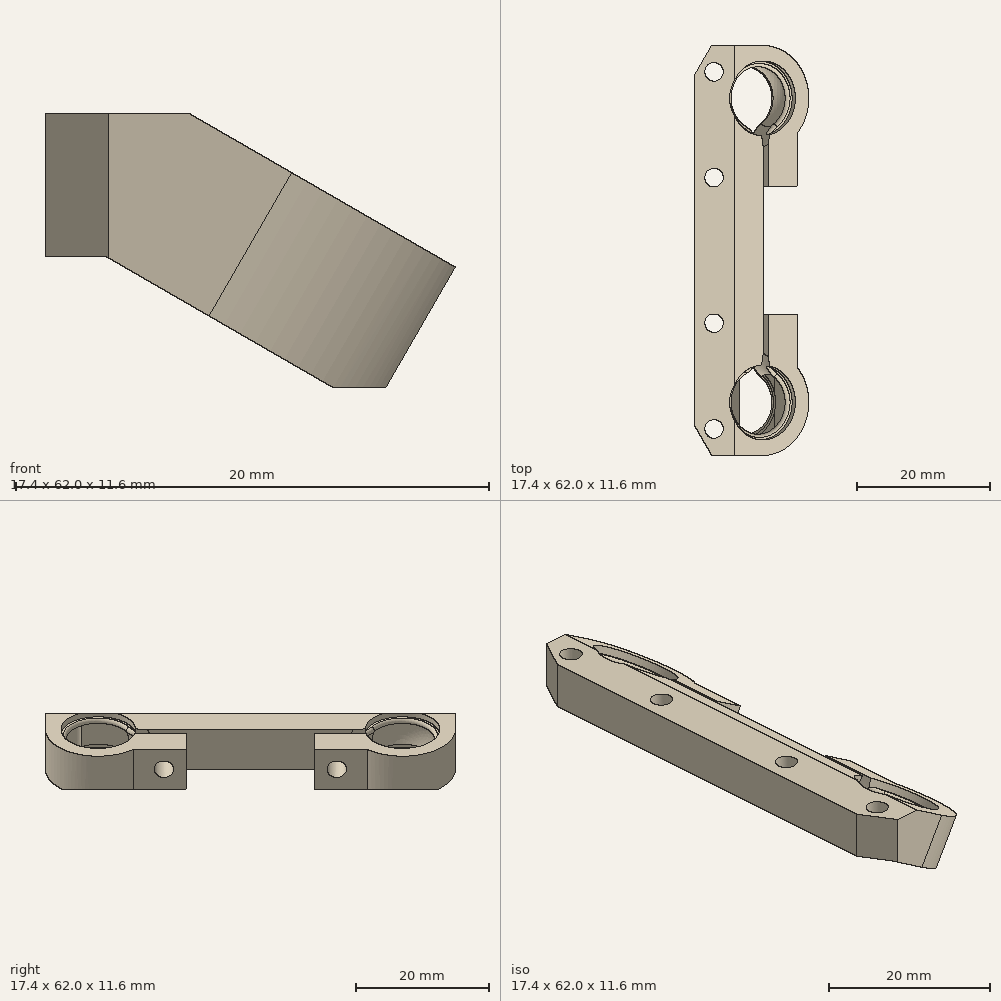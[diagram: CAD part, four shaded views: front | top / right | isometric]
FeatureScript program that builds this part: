
annotation { "Feature Type Name" : "Feature", "Feature Type Description" : "" }
export const myFeature = defineFeature(function(context is Context, id is Id, definition is map)
    precondition{}
    {
        {
            assignVariable(context, id + "F0", {"name" : "balld", "anyValue" : 10});
        }
        {
            assignVariable(context, id + "F1", {"name" : "bushd", "anyValue" : 8});
        }
        {
            var Q0;
            Q0=qCreatedBy(makeId("Top.planeOp"),FACE);
            var sketch = newSketch(context, id + "F2", { "sketchPlane" : qUnion([Q0])});
            skLineSegment(sketch, "E0", {"start": v(0, -23) * mm, "end": v(0, 23) * mm});
            skCircle(sketch, "E1", {"center": v(0, -23) * mm, "radius": 5.15 * mm});
            skArc(sketch, "E2", {"start": v(0, -31) * mm, "mid": v(7.31, -26.24) * mm, "end": v(5.92, -17.62) * mm});
            skLineSegment(sketch, "E3", {"start": v(-5.15, -23) * mm, "end": v(5.15, -23) * mm});
            skLineSegment(sketch, "E4", {"start": v(-8, -23) * mm, "end": v(-8, 0) * mm});
            skLineSegment(sketch, "E5", {"start": v(-8, 0) * mm, "end": v(0, 0) * mm});
            skLineSegment(sketch, "E6", {"start": v(0, -9.62) * mm, "end": v(5.92, -9.62) * mm});
            skLineSegment(sketch, "E7", {"start": v(5.92, -9.62) * mm, "end": v(5.92, -17.62) * mm});
            skLineSegment(sketch, "E8", {"start": v(1, -23) * mm, "end": v(1, -9.62) * mm});
            skCircle(sketch, "E9.0", {"center": v(0, -23) * mm, "radius": 5.65 * mm});
            skLineSegment(sketch, "E10", {"start": v(-8, -23) * mm, "end": v(-8, -31) * mm});
            skLineSegment(sketch, "E11", {"start": v(-8, -31) * mm, "end": v(2.55, -31) * mm});
            skSolve(sketch);
        }
        {
            var Q0;
            Q0=makeQuery(id+"F2.imprint","IMPRINT",FACE,{"disambiguationData":[TD([[makeQuery(id+"F2.imprint","IMPRINT",EDGE,{"derivedFrom":sQuery(id+"F2.wireOp",EDGE,"E2")}),1.0]])]});
            var Q1;
            {var subQ0=sQuery(id+"F2.wireOp",EDGE,"E3");Q1=makeQuery(id+"F2.imprint","IMPRINT",FACE,{"disambiguationData":[TD([[makeQuery(id+"F2.imprint","IMPRINT",EDGE,{"derivedFrom":subQ0}),1.0]])]});}
            var Q2;
            {var subQ0=sQuery(id+"F2.wireOp",EDGE,"E3");Q2=makeQuery(id+"F2.imprint","IMPRINT",FACE,{"disambiguationData":[TD([[makeQuery(id+"F2.imprint","IMPRINT",EDGE,{"derivedFrom":subQ0}),-1.0]])]});}
            var Q3;
            {var subQ0=sQuery(id+"F2.wireOp",EDGE,"0A8tKCgS-ejaw-YyMs-Dn46-rruMUtFQQFLV");Q3=makeQuery(id+"F2.imprint","IMPRINT",FACE,{"disambiguationData":[TD([[makeQuery(id+"F2.imprint","IMPRINT",EDGE,{"derivedFrom":subQ0}),1.0]])]});}
            var Q4;
            {var subQ1=sQuery(id+"F2.wireOp",EDGE,"E1");var subQ8=sQuery(id+"F2.wireOp",EDGE,"E0");var subQ9=makeQuery(id+"F2.imprint","INTERSECT",VERTEX,{"derivedFrom":[subQ8,subQ1]});Q4=makeQuery(id+"F2.imprint","IMPRINT",FACE,{"disambiguationData":[TD([[makeQuery(id+"F2.imprint","IMPRINT",EDGE,{"disambiguationData":[TD([[subQ9,-1.0]])],"derivedFrom":subQ8}),1.0]])]});}
            extrude(context, id + "F3", {"entities" : qUnion([Q0, Q1, Q2, Q3, Q4]), "endBound" : BoundingType.SYMMETRIC, "depth" : (getVariable(context, 'balld') / 2) * mm});
        }
        {
            var Q0;
            Q0=makeQuery(id+"F2.imprint","IMPRINT",FACE,{"disambiguationData":[TD([[makeQuery(id+"F2.imprint","IMPRINT",EDGE,{"derivedFrom":sQuery(id+"F2.wireOp",EDGE,"E2")}),1.0]])]});
            extrude(context, id + "F4", {"entities" : qUnion([Q0]), "operationType" : NewBodyOperationType.ADD, "endBound" : BoundingType.SYMMETRIC, "depth" : 7 * mm});
        }
        {
            var Q0;
            {var subQ0=sQuery(id+"F2.wireOp",EDGE,"E7");Q0=makeQuery(id+"F4.boolean.opBoolean","MERGE",FACE,{"derivedFrom":[makeQuery(id+"F3.opExtrude","SWEPT_FACE",FACE,{"disambiguationData":[OSD([subQ0])]}),makeQuery(id+"F4.opExtrude","SWEPT_FACE",FACE,{"disambiguationData":[OSD([subQ0])]})]});}
            var sketch = newSketch(context, id + "F5", { "sketchPlane" : qUnion([Q0])});
            skCircle(sketch, "E12", {"center": v(-13.07, 0) * mm, "radius": 1.45 * mm});
            skPoint(sketch, "E12.centerSnap0", {"position": v(-9.62, 0) * mm});
            skSolve(sketch);
        }
        {
            var Q0;
            Q0=makeQuery(id+"F5.imprint","IMPRINT",FACE,{"disambiguationData":[TD([[makeQuery(id+"F5.imprint","IMPRINT",EDGE,{"derivedFrom":sQuery(id+"F5.wireOp",EDGE,"E12")}),1.0]])]});
            extrude(context, id + "F6", {"entities" : qUnion([Q0]), "operationType" : NewBodyOperationType.REMOVE, "oppositeDirection" : true, "depth" : 11 * mm});
        }
        {
            var Q0;
            {var subQ0=sQuery(id+"F2.wireOp",EDGE,"E5");Q0=makeQuery(id+"F4.boolean.opBoolean","MERGE",FACE,{"derivedFrom":[makeQuery(id+"F3.opExtrude","SWEPT_FACE",FACE,{"disambiguationData":[OSD([subQ0])]}),makeQuery(id+"F4.opExtrude","SWEPT_FACE",FACE,{"disambiguationData":[OSD([subQ0])]})]});}
            var sketch = newSketch(context, id + "F7", { "sketchPlane" : qUnion([Q0])});
            skCircle(sketch, "E13", {"center": v(0, 0) * mm, "radius": 16.02 * mm});
            skSolve(sketch);
        }
        {
            var Q0;
            Q0=makeQuery(id+"F3.opExtrude","SWEPT_BODY",BODY,{"disambiguationData":[OSD([sQuery(id+"F2.wireOp",EDGE,"E0"),sQuery(id+"F2.wireOp",EDGE,"E2"),sQuery(id+"F2.wireOp",EDGE,"E3"),sQuery(id+"F2.wireOp",EDGE,"E4"),sQuery(id+"F2.wireOp",EDGE,"E5"),sQuery(id+"F2.wireOp",EDGE,"E6"),sQuery(id+"F2.wireOp",EDGE,"E7"),sQuery(id+"F2.wireOp",EDGE,"E8"),sQuery(id+"F2.wireOp",EDGE,"E10"),sQuery(id+"F2.wireOp",EDGE,"E11")])]});
            var Q1;
            Q1=sQuery(id+"F7.wireOp",EDGE,"E13");
            transform(context, id + "F8", {"entities" : qUnion([Q0]), "transformType" : TransformType.ROTATION, "transformAxis" : qUnion([Q1]), "angle" : 30 * degree, "makeCopy" : false});
        }
        {
            var Q0;
            {var subQ0=sQuery(id+"F2.wireOp",EDGE,"E5");Q0=makeQuery(id+"F4.boolean.opBoolean","MERGE",FACE,{"derivedFrom":[makeQuery(id+"F3.opExtrude","SWEPT_FACE",FACE,{"disambiguationData":[OSD([subQ0])]}),makeQuery(id+"F4.opExtrude","SWEPT_FACE",FACE,{"disambiguationData":[OSD([subQ0])]})]});}
            var sketch = newSketch(context, id + "F9", { "sketchPlane" : qUnion([Q0])});
            skLineSegment(sketch, "E14", {"start": v(-6.5, -6.08) * mm, "end": v(8.68, -6.08) * mm});
            skLineSegment(sketch, "E15", {"start": v(8.68, -6.08) * mm, "end": v(8.68, 5.56) * mm});
            skLineSegment(sketch, "E16", {"start": v(8.68, 5.56) * mm, "end": v(2.63, 5.56) * mm});
            skLineSegment(sketch, "E17", {"start": v(1.75, -3.03) * mm, "end": v(1.75, -6.08) * mm});
            skLineSegment(sketch, "E18.0", {"start": v(-5.18, -7.03) * mm, "end": v(1.75, -3.03) * mm});
            skLineSegment(sketch, "E19", {"start": v(-5.18, -7.03) * mm, "end": v(-8.68, -0.97) * mm});
            skSolve(sketch);
        }
        {
            var Q0;
            {var subQ3=sQuery(id+"F9.wireOp",EDGE,"E17");Q0=makeQuery(id+"F9.imprint","IMPRINT",FACE,{"disambiguationData":[TD([[makeQuery(id+"F9.imprint","IMPRINT",EDGE,{"derivedFrom":subQ3}),1.0]])]});}
            var Q1;
            {var subQ0=sQuery(id+"F9.wireOp",EDGE,"E15");var subQ5=sQuery(id+"F9.wireOp",EDGE,"E16");var subQ6=makeQuery(id+"F9.imprint","INTERSECT",VERTEX,{"derivedFrom":[subQ0,subQ5]});Q1=makeQuery(id+"F9.imprint","IMPRINT",FACE,{"disambiguationData":[TD([[makeQuery(id+"F9.imprint","IMPRINT",EDGE,{"disambiguationData":[TD([[subQ6,-1.0]])],"derivedFrom":subQ5}),1.0]])]});}
            var Q2;
            {var subQ0=sQuery(id+"F2.wireOp",EDGE,"E11");Q2=makeQuery(id+"F4.boolean.opBoolean","MERGE",FACE,{"derivedFrom":[makeQuery(id+"F3.opExtrude","SWEPT_FACE",FACE,{"disambiguationData":[OSD([subQ0])]}),makeQuery(id+"F4.opExtrude","SWEPT_FACE",FACE,{"disambiguationData":[OSD([subQ0])]})]});}
            extrude(context, id + "F10", {"entities" : qUnion([Q0, Q1]), "operationType" : NewBodyOperationType.ADD, "endBound" : BoundingType.UP_TO_SURFACE, "oppositeDirection" : true, "endBoundEntityFace" : qUnion([Q2]), "depth" : (30 + getVariable(context, 'bushd')) * mm});
        }
        {
            var Q0;
            {var subQ0=sQuery(id+"F2.wireOp",EDGE,"E3");var subQ1=sQuery(id+"F2.wireOp",EDGE,"E1");var subQ2=makeQuery(id+"F2.imprint","INTERSECT",VERTEX,{"disambiguationData":[OD(0.0)],"derivedFrom":[subQ1,subQ0]});Q0=makeQuery(id+"F2.imprint","IMPRINT",FACE,{"disambiguationData":[TD([[makeQuery(id+"F2.imprint","IMPRINT",EDGE,{"disambiguationData":[TD([[subQ2,-1.0]])],"derivedFrom":subQ1}),1.0]])]});}
            var Q1;
            Q1=sQuery(id+"F2.wireOp",EDGE,"E3");
            revolve(context, id + "F11", {"operationType" : NewBodyOperationType.REMOVE, "entities" : qUnion([Q0]), "axis" : qUnion([Q1]), "revolveType" : RevolveType.FULL, "oppositeDirection" : true});
        }
        {
            var Q0;
            {var subQ0=sQuery(id+"F2.wireOp",EDGE,"E3");var subQ1=sQuery(id+"F2.wireOp",EDGE,"E1");var subQ2=makeQuery(id+"F2.imprint","INTERSECT",VERTEX,{"disambiguationData":[OD(0.0)],"derivedFrom":[subQ1,subQ0]});Q0=makeQuery(id+"F2.imprint","IMPRINT",FACE,{"disambiguationData":[TD([[makeQuery(id+"F2.imprint","IMPRINT",EDGE,{"disambiguationData":[TD([[subQ2,-1.0]])],"derivedFrom":subQ1}),1.0]])]});}
            var Q1;
            Q1=sQuery(id+"F2.wireOp",EDGE,"E3");
            revolve(context, id + "F12", {"entities" : qUnion([Q0]), "axis" : qUnion([Q1]), "revolveType" : RevolveType.FULL});
        }
        {
            var Q0;
            Q0=makeQuery(id+"F11.boolean.opBoolean","INTERSECT",EDGE,{"derivedFrom":[makeQuery(id+"F3.opExtrude","SWEPT_FACE",FACE,{"disambiguationData":[OSD([sQuery(id+"F2.wireOp",EDGE,"E0")])]}),makeQuery(id+"F11.opRevolve","SWEPT_FACE",FACE,{"disambiguationData":[OSD([sQuery(id+"F2.wireOp",EDGE,"E1")])]})]});
            var Q1;
            Q1=makeQuery(id+"F11.boolean.opBoolean","INTERSECT",EDGE,{"derivedFrom":[makeQuery(id+"F3.opExtrude","SWEPT_FACE",FACE,{"disambiguationData":[OSD([sQuery(id+"F2.wireOp",EDGE,"E8")])]}),makeQuery(id+"F11.opRevolve","SWEPT_FACE",FACE,{"disambiguationData":[OSD([sQuery(id+"F2.wireOp",EDGE,"E1")])]})]});
            fillet(context, id + "F13", {"entities" : qUnion([Q0, Q1]), "radius" : 4 * mm, "tangentPropagation" : true, "allowEdgeOverflow" : false});
        }
        {
            var Q0;
            {var subQ0=sQuery(id+"F9.wireOp",EDGE,"E16");var subQ1=sQuery(id+"F2.wireOp",EDGE,"E5");var subQ2=makeQuery(id+"F4.opExtrude","CAP_EDGE",EDGE,{"disambiguationData":[OSD([subQ1])],"isStart":false});var subQ3=makeQuery(id+"F9.imprint","INTERSECT",VERTEX,{"derivedFrom":[subQ2,subQ0]});Q0=makeQuery(id+"F9.imprint","IMPRINT",FACE,{"disambiguationData":[TD([[makeQuery(id+"F9.imprint","IMPRINT",EDGE,{"disambiguationData":[TD([[subQ3,1.0]])],"derivedFrom":subQ0}),-1.0]])]});}
            var Q1;
            {var subQ0=sQuery(id+"F9.wireOp",EDGE,"E19");var subQ1=sQuery(id+"F9.wireOp",EDGE,"E14");var subQ2=makeQuery(id+"F9.imprint","INTERSECT",VERTEX,{"derivedFrom":[subQ1,subQ0]});Q1=makeQuery(id+"F9.imprint","IMPRINT",FACE,{"disambiguationData":[TD([[makeQuery(id+"F9.imprint","IMPRINT",EDGE,{"disambiguationData":[TD([[subQ2,-1.0]])],"derivedFrom":subQ1}),-1.0]])]});}
            extrude(context, id + "F14", {"entities" : qUnion([Q0, Q1]), "operationType" : NewBodyOperationType.REMOVE, "oppositeDirection" : true, "depth" : 46.37 * mm});
        }
        {
            var Q0;
            Q0=makeQuery(id+"F11.boolean.opBoolean","INTERSECT",EDGE,{"derivedFrom":[makeQuery(id+"F3.opExtrude","CAP_FACE",FACE,{"disambiguationData":[OSD([sQuery(id+"F2.wireOp",EDGE,"E0"),sQuery(id+"F2.wireOp",EDGE,"E2"),sQuery(id+"F2.wireOp",EDGE,"E3"),sQuery(id+"F2.wireOp",EDGE,"E4"),sQuery(id+"F2.wireOp",EDGE,"E5"),sQuery(id+"F2.wireOp",EDGE,"E6"),sQuery(id+"F2.wireOp",EDGE,"E7"),sQuery(id+"F2.wireOp",EDGE,"E8")])],"isStart":true}),makeQuery(id+"F11.opRevolve","SWEPT_FACE",FACE,{"disambiguationData":[OSD([sQuery(id+"F2.wireOp",EDGE,"E1")])]})]});
            var Q1;
            Q1=makeQuery(id+"F11.boolean.opBoolean","INTERSECT",EDGE,{"derivedFrom":[makeQuery(id+"F3.opExtrude","CAP_FACE",FACE,{"disambiguationData":[OSD([sQuery(id+"F2.wireOp",EDGE,"E0"),sQuery(id+"F2.wireOp",EDGE,"E2"),sQuery(id+"F2.wireOp",EDGE,"E3"),sQuery(id+"F2.wireOp",EDGE,"E4"),sQuery(id+"F2.wireOp",EDGE,"E5"),sQuery(id+"F2.wireOp",EDGE,"E6"),sQuery(id+"F2.wireOp",EDGE,"E7"),sQuery(id+"F2.wireOp",EDGE,"E8")])],"isStart":false}),makeQuery(id+"F11.opRevolve","SWEPT_FACE",FACE,{"disambiguationData":[OSD([sQuery(id+"F2.wireOp",EDGE,"E1")])]})]});
            var Q2;
            Q2=makeQuery(id+"F10.opExtrude","SWEPT_EDGE",EDGE,{"disambiguationData":[OSD([sQuery(id+"F2.wireOp",EDGE,"E5"),sQuery(id+"F9.wireOp",EDGE,"jgZU3u5d-GVGD-WIfK-WW3S-JiZfo5GlXRWX"),sQuery(id+"F9.wireOp",EDGE,"RI7zuHdH-Aulu-Pmv9-ypUC-siWLOt7I26mh")])]});
            var Q3;
            Q3=makeQuery(id+"FphnwMnj7a8bU9b_2.opExtrude","SWEPT_EDGE",EDGE,{"disambiguationData":[OSD([sQuery(id+"F2.wireOp",EDGE,"E2"),sQuery(id+"F2.wireOp",EDGE,"E11"),sQuery(id+"FRQjfZNPT5smCK5_2.wireOp",EDGE,"EvZcPotD-z7jL-Qfjt-3erJ-b1LS2jvMAbUN")])]});
            fillet(context, id + "F15", {"entities" : qUnion([Q0, Q1, Q2, Q3]), "radius" : 0.5 * mm, "tangentPropagation" : true, "allowEdgeOverflow" : false});
        }
        {
            var Q0;
            {var subQ0=sQuery(id+"F9.wireOp",EDGE,"E15");var subQ1=sQuery(id+"F2.wireOp",EDGE,"E5");var subQ2=sQuery(id+"F2.wireOp",EDGE,"E11");Q0=makeQuery(id+"F10.boolean.opBoolean","MERGE",FACE,{"derivedFrom":[makeQuery(id+"F4.boolean.opBoolean","MERGE",FACE,{"derivedFrom":[makeQuery(id+"F3.opExtrude","SWEPT_FACE",FACE,{"disambiguationData":[OSD([subQ2])]}),makeQuery(id+"F4.opExtrude","SWEPT_FACE",FACE,{"disambiguationData":[OSD([subQ2])]})]}),makeQuery(id+"F10.opExtrude","CAP_FACE",FACE,{"disambiguationData":[OSD([subQ1,sQuery(id+"F9.wireOp",EDGE,"E14"),subQ0,sQuery(id+"F9.wireOp",EDGE,"E17")])],"isStart":false}),makeQuery(id+"F10.opExtrude","CAP_FACE",FACE,{"disambiguationData":[OSD([sQuery(id+"F2.wireOp",EDGE,"E4"),subQ1,subQ0,sQuery(id+"F9.wireOp",EDGE,"E16")])],"isStart":false})]});}
            var sketch = newSketch(context, id + "F16", { "sketchPlane" : qUnion([Q0])});
            skLineSegment(sketch, "E20", {"start": v(-1.75, -3.03) * mm, "end": v(-8.68, 0.97) * mm});
            skLineSegment(sketch, "E21.0", {"start": v(3.64, -5) * mm, "end": v(-6.14, 0.66) * mm});
            skLineSegment(sketch, "E22", {"start": v(-6.14, 0.66) * mm, "end": v(-6.14, -6.08) * mm});
            skLineSegment(sketch, "E23", {"start": v(-6.14, -0.5) * mm, "end": v(-8.68, -0.5) * mm});
            skSolve(sketch);
        }
        {
            var Q0;
            {var subQ1=makeQuery(id+"F10.opExtrude","CAP_EDGE",EDGE,{"disambiguationData":[OSD([sQuery(id+"F9.wireOp",EDGE,"E17")])],"isStart":false});Q0=makeQuery(id+"F16.imprint","IMPRINT",FACE,{"disambiguationData":[TD([[makeQuery(id+"F16.imprint","IMPRINT",EDGE,{"derivedFrom":subQ1}),1.0]])]});}
            var Q1;
            {var subQ4=sQuery(id+"F16.wireOp",EDGE,"E23");Q1=makeQuery(id+"F16.imprint","IMPRINT",FACE,{"disambiguationData":[TD([[makeQuery(id+"F16.imprint","IMPRINT",EDGE,{"derivedFrom":subQ4}),1.0]])]});}
            extrude(context, id + "F17", {"entities" : qUnion([Q0, Q1]), "operationType" : NewBodyOperationType.REMOVE, "oppositeDirection" : true, "depth" : 34.92 * mm});
        }
        {
            var Q0;
            {var subQ0=sQuery(id+"F9.wireOp",EDGE,"E16");Q0=makeQuery(id+"F14.boolean.opBoolean","MERGE",FACE,{"derivedFrom":[makeQuery(id+"F10.opExtrude","SWEPT_FACE",FACE,{"disambiguationData":[OSD([subQ0])]})],"fromTools":[makeQuery(id+"F14.opExtrude","SWEPT_FACE",FACE,{"disambiguationData":[OSD([subQ0])]})]});}
            var sketch = newSketch(context, id + "F18", { "sketchPlane" : qUnion([Q0])});
            skCircle(sketch, "E24", {"center": v(-5.66, -27) * mm, "radius": 1.4 * mm});
            skPoint(sketch, "E24.centerSnap0", {"position": v(-5.66, -31) * mm});
            skCircle(sketch, "E25", {"center": v(-5.66, -11) * mm, "radius": 1.4 * mm});
            skCircle(sketch, "E26", {"center": v(0, -23) * mm, "radius": 5.15 * mm, "construction": true});
            skSolve(sketch);
        }
        {
            var Q0;
            Q0=makeQuery(id+"F18.imprint","IMPRINT",FACE,{"disambiguationData":[TD([[makeQuery(id+"F18.imprint","IMPRINT",EDGE,{"derivedFrom":sQuery(id+"F18.wireOp",EDGE,"E24")}),1.0]])]});
            var Q1;
            Q1=makeQuery(id+"F18.imprint","IMPRINT",FACE,{"disambiguationData":[TD([[makeQuery(id+"F18.imprint","IMPRINT",EDGE,{"derivedFrom":sQuery(id+"F18.wireOp",EDGE,"E25")}),1.0]])]});
            extrude(context, id + "F19", {"entities" : qUnion([Q0, Q1]), "operationType" : NewBodyOperationType.REMOVE, "oppositeDirection" : true, "depth" : 25 * mm});
        }
        {
            var Q0;
            Q0=makeQuery(id+"F3.opExtrude","SWEPT_BODY",BODY,{"disambiguationData":[OSD([sQuery(id+"F2.wireOp",EDGE,"E0"),sQuery(id+"F2.wireOp",EDGE,"E2"),sQuery(id+"F2.wireOp",EDGE,"E3"),sQuery(id+"F2.wireOp",EDGE,"E4"),sQuery(id+"F2.wireOp",EDGE,"E5"),sQuery(id+"F2.wireOp",EDGE,"E6"),sQuery(id+"F2.wireOp",EDGE,"E7"),sQuery(id+"F2.wireOp",EDGE,"E8"),sQuery(id+"F2.wireOp",EDGE,"E10"),sQuery(id+"F2.wireOp",EDGE,"E11")])]});
            var Q1;
            {var subQ0=sQuery(id+"F2.wireOp",EDGE,"E5");var subQ6=makeQuery(id+"F4.opExtrude","CAP_EDGE",EDGE,{"disambiguationData":[OSD([subQ0])],"isStart":true});Q1=makeQuery(id+"F9.imprint","IMPRINT",FACE,{"disambiguationData":[TD([[makeQuery(id+"F9.imprint","IMPRINT",EDGE,{"derivedFrom":subQ6}),-1.0]])]});}
            mirror(context, id + "F20", {"operationType" : NewBodyOperationType.ADD, "entities" : qUnion([Q0]), "mirrorPlane" : qUnion([Q1])});
        }
        {
            var Q0;
            {var subQ0=sQuery(id+"F9.wireOp",EDGE,"E16");var subQ1=makeQuery(id+"F14.boolean.opBoolean","MERGE",FACE,{"derivedFrom":[makeQuery(id+"F10.opExtrude","SWEPT_FACE",FACE,{"disambiguationData":[OSD([subQ0])]})],"fromTools":[makeQuery(id+"F14.opExtrude","SWEPT_FACE",FACE,{"disambiguationData":[OSD([subQ0])]})]});Q0=makeQuery(id+"F20.boolean.opBoolean","MERGE",FACE,{"derivedFrom":[subQ1,makeQuery(id+"F20.opPattern","COPY",FACE,{"derivedFrom":subQ1,"instanceName":"1"})]});}
            var sketch = newSketch(context, id + "F21", { "sketchPlane" : qUnion([Q0])});
            skCircle(sketch, "E27", {"center": v(-24, 0) * mm, "radius": 23.45 * mm});
            skPoint(sketch, "E27.centerSnap0", {"position": v(-8.68, 0) * mm});
            skCircle(sketch, "E28", {"center": v(0, -23) * mm, "radius": 5.15 * mm});
            skSolve(sketch);
        }
        {
            var Q0;
            {var subQ0=sQuery(id+"F9.wireOp",EDGE,"E16");var subQ1=makeQuery(id+"F14.boolean.opBoolean","MERGE",FACE,{"derivedFrom":[makeQuery(id+"F10.opExtrude","SWEPT_FACE",FACE,{"disambiguationData":[OSD([subQ0])]})],"fromTools":[makeQuery(id+"F14.opExtrude","SWEPT_FACE",FACE,{"disambiguationData":[OSD([subQ0])]})]});Q0=makeQuery(id+"F20.boolean.opBoolean","MERGE",FACE,{"derivedFrom":[subQ1,makeQuery(id+"F20.opPattern","COPY",FACE,{"derivedFrom":subQ1,"instanceName":"1"})]});}
            var sketch = newSketch(context, id + "F22", { "sketchPlane" : qUnion([Q0])});
            skLineSegment(sketch, "E29.0", {"start": v(-8.68, -31) * mm, "end": v(-8.68, 31) * mm});
            skLineSegment(sketch, "E30.0", {"start": v(-2.63, 31) * mm, "end": v(-8.68, 31) * mm});
            skLineSegment(sketch, "E31", {"start": v(-6, 31) * mm, "end": v(-8.68, 26.4) * mm});
            skLineSegment(sketch, "E32", {"start": v(-8.68, 0) * mm, "end": v(-2.63, 0) * mm});
            skLineSegment(sketch, "E33.MirrorCS", {"start": v(-6, -31) * mm, "end": v(-8.68, -26.4) * mm});
            skSolve(sketch);
        }
        {
            var Q0;
            {var subQ3=sQuery(id+"F22.wireOp",EDGE,"E31");Q0=makeQuery(id+"F22.imprint","IMPRINT",FACE,{"disambiguationData":[TD([[makeQuery(id+"F22.imprint","IMPRINT",EDGE,{"derivedFrom":subQ3}),-1.0]])]});}
            var Q1;
            {var subQ7=sQuery(id+"F22.wireOp",EDGE,"E33.MirrorCS");Q1=makeQuery(id+"F22.imprint","IMPRINT",FACE,{"disambiguationData":[TD([[makeQuery(id+"F22.imprint","IMPRINT",EDGE,{"derivedFrom":subQ7}),1.0]])]});}
            extrude(context, id + "F23", {"entities" : qUnion([Q0, Q1]), "operationType" : NewBodyOperationType.REMOVE, "oppositeDirection" : true, "depth" : 25 * mm});
        }
    });
